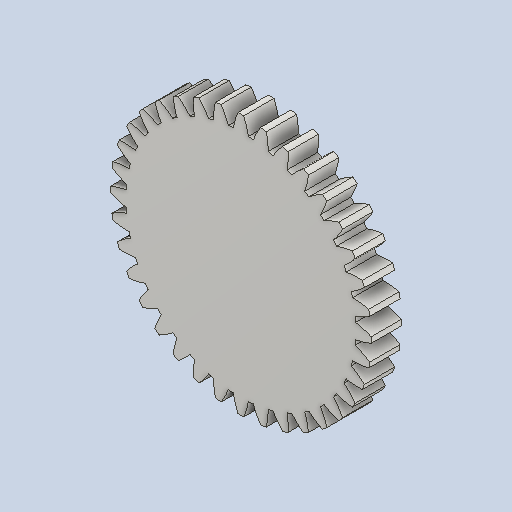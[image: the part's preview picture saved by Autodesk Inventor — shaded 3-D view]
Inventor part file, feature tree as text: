
AUTODESK INVENTOR PART (.ipt)
format: ipt  version: 2024 (Build 280153000, 153)  size: 285,696 bytes
history: native  units: mm (DEFAULTED — no unit token found)
features: plane x3, other x3, extrude x1, sketch x1
ambient origin geometry x8: Origin, YZ Plane, XZ Plane, XY Plane, X Axis, Y Axis, Z Axis, Center Point
bodies: Solid1 (feature_tree)
feature tree (8):
  extrude  "Extrusion1"  Depth=20.0mm TaperAngle=0.0deg
  plane  "Work Plane2"
  plane  "Work Plane8"
  plane  "Work Plane9"
  other  "Spur Gear"
  sketch  "Sketch1"  dims[d0=172.0mm d1=20.0mm d2=0.0mm d3=162.0mm d4=10.0mm d5=0.0mm d16=140.0mm d17=0.0mm d34=0.872665mm d39=0.0mm d41=0.0mm d43=140.0mm d46=140.0mm d47=0.0mm d48=0.0mm]
  other  "Srf1"
  other  "Pitch Diameter"
